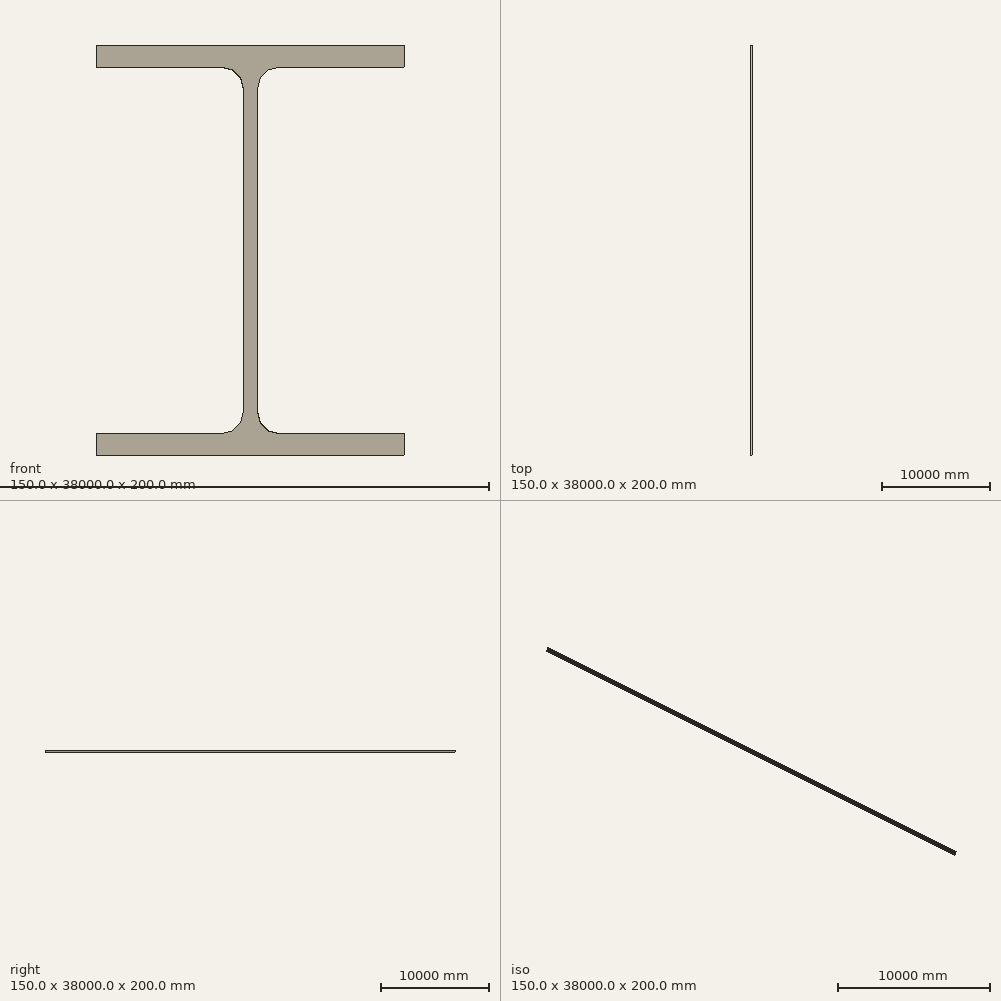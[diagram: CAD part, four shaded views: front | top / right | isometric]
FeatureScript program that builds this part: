
annotation { "Feature Type Name" : "Feature", "Feature Type Description" : "" }
export const myFeature = defineFeature(function(context is Context, id is Id, definition is map)
    precondition{}
    {
        {
            var Q0;
            Q0=qCreatedBy(makeId("Front.planeOp"),FACE);
            var sketch = newSketch(context, id + "F0", { "sketchPlane" : qUnion([Q0])});
            skLineSegment(sketch, "E0.left", {"start": v(3.55, 79.3) * mm, "end": v(3.55, -79.3) * mm});
            skLineSegment(sketch, "E0.right", {"start": v(-3.55, 79.3) * mm, "end": v(-3.55, -79.3) * mm});
            skPoint(sketch, "E0.middle", {"position": v(0, 0) * mm});
            skLineSegment(sketch, "E1.bottom", {"start": v(-75, 89.3) * mm, "end": v(-13.55, 89.3) * mm});
            skLineSegment(sketch, "E1.top", {"start": v(-75, 100) * mm, "end": v(75, 100) * mm});
            skLineSegment(sketch, "E1.left", {"start": v(-75, 89.3) * mm, "end": v(-75, 100) * mm});
            skLineSegment(sketch, "E1.right", {"start": v(75, 89.3) * mm, "end": v(75, 100) * mm});
            skLineSegment(sketch, "E2.bottom", {"start": v(75, -89.3) * mm, "end": v(13.55, -89.3) * mm});
            skLineSegment(sketch, "E2.top", {"start": v(75, -100) * mm, "end": v(-75, -100) * mm});
            skLineSegment(sketch, "E2.left", {"start": v(75, -89.3) * mm, "end": v(75, -100) * mm});
            skLineSegment(sketch, "E2.right", {"start": v(-75, -89.3) * mm, "end": v(-75, -100) * mm});
            skLineSegment(sketch, "E3.trimOffspring", {"start": v(13.55, 89.3) * mm, "end": v(75, 89.3) * mm});
            skLineSegment(sketch, "E4.trimOffspring", {"start": v(-13.55, -89.3) * mm, "end": v(-75, -89.3) * mm});
            skPoint(sketch, "E5.visualSharp", {"position": v(3.55, 89.3) * mm});
            skArc(sketch, "E5.filletArc", {"start": v(13.55, 89.3) * mm, "mid": v(6.48, 86.37) * mm, "end": v(3.55, 79.3) * mm});
            skPoint(sketch, "E6.visualSharp", {"position": v(-3.55, 89.3) * mm});
            skArc(sketch, "E6.filletArc", {"start": v(-3.55, 79.3) * mm, "mid": v(-6.48, 86.37) * mm, "end": v(-13.55, 89.3) * mm});
            skPoint(sketch, "E7.visualSharp", {"position": v(3.55, -89.3) * mm});
            skArc(sketch, "E7.filletArc", {"start": v(3.55, -79.3) * mm, "mid": v(6.48, -86.37) * mm, "end": v(13.55, -89.3) * mm});
            skPoint(sketch, "E8.visualSharp", {"position": v(-3.55, -89.3) * mm});
            skArc(sketch, "E8.filletArc", {"start": v(-13.55, -89.3) * mm, "mid": v(-6.48, -86.37) * mm, "end": v(-3.55, -79.3) * mm});
            skSolve(sketch);
        }
        {
            var Q0;
            Q0=qSketchRegion(id+"F0",true);
            extrude(context, id + "F1", {"entities" : qUnion([Q0]), "oppositeDirection" : true, "depth" : 38000 * mm});
        }
    });
